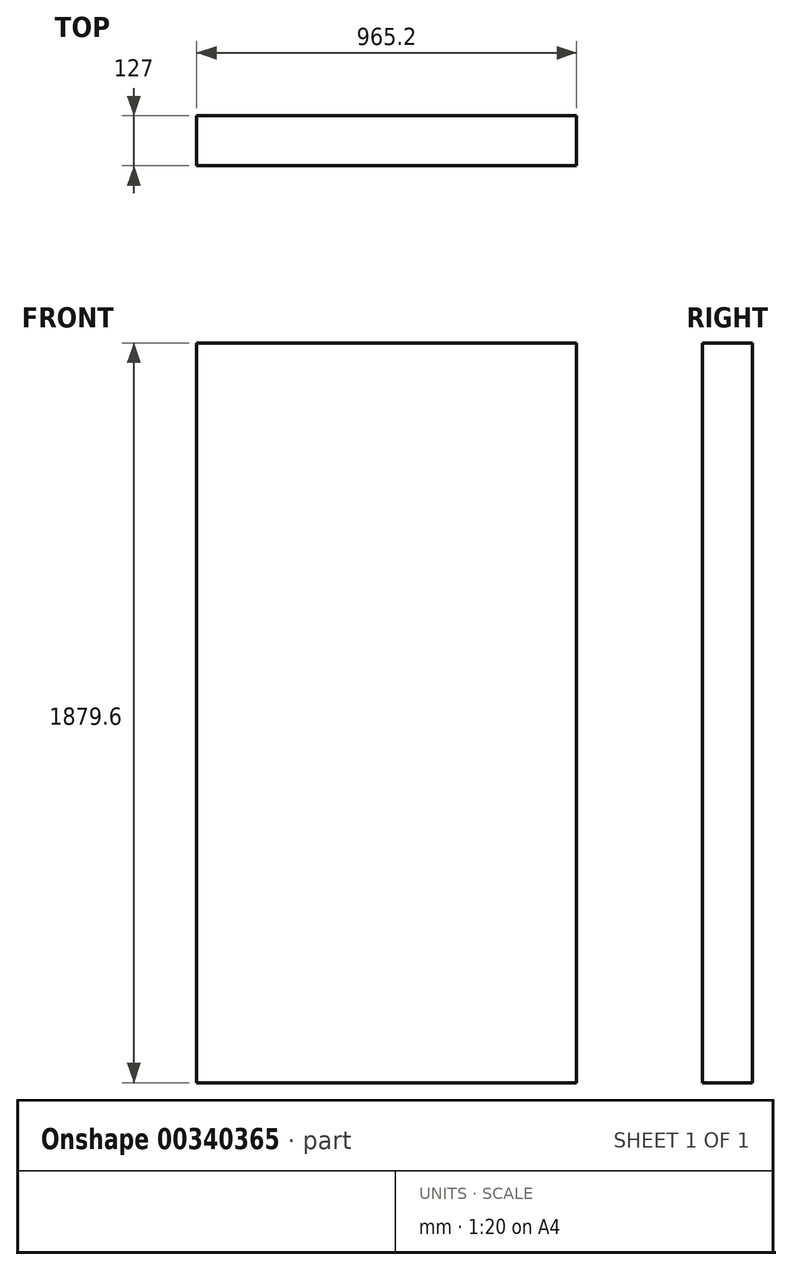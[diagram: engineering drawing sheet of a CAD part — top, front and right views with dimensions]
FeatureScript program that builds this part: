
annotation { "Feature Type Name" : "Feature", "Feature Type Description" : "" }
export const myFeature = defineFeature(function(context is Context, id is Id, definition is map)
    precondition{}
    {
        {
            var Q0;
            Q0=qCreatedBy(makeId("Front.planeOp"),FACE);
            var sketch = newSketch(context, id + "F0", { "sketchPlane" : qUnion([Q0])});
            skLineSegment(sketch, "E0.bottom", {"start": v(-482.6, 939.8) * mm, "end": v(482.6, 939.8) * mm});
            skLineSegment(sketch, "E0.top", {"start": v(-482.6, -939.8) * mm, "end": v(482.6, -939.8) * mm});
            skLineSegment(sketch, "E0.left", {"start": v(-482.6, 939.8) * mm, "end": v(-482.6, -939.8) * mm});
            skLineSegment(sketch, "E0.right", {"start": v(482.6, 939.8) * mm, "end": v(482.6, -939.8) * mm});
            skPoint(sketch, "E0.middle", {"position": v(0, 0) * mm});
            skSolve(sketch);
        }
        {
            var Q0;
            Q0=makeQuery(id+"F0.imprint","IMPRINT",FACE,{"disambiguationData":[TD([[makeQuery(id+"F0.imprint","IMPRINT",EDGE,{"derivedFrom":sQuery(id+"F0.wireOp",EDGE,"E0.bottom")}),-1.0]])]});
            extrude(context, id + "F1", {"entities" : qUnion([Q0]), "oppositeDirection" : true, "depth" : 127 * mm});
        }
    });
